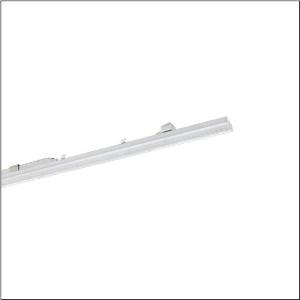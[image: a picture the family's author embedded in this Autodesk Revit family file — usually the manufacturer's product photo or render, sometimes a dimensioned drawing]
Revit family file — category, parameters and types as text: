
# Revit family: tl_l_5wd7a8p0g2b5
name_source: partatom
category: Lighting Fixtures
units: mm (PartAtom-declared; Revit-internal decimal feet)

## family parameters
Cut with Voids When Loaded = No
Host = Face
Light Source = No
Part Type = Normal
Room Calculation Point = No
Round Connector Dimension = Use Diameter
Shared = No

## types (1)
- --- (1 x LED, 5000 lm, 31.5 W, 4000K)
    Apparent Load = 32 VA
    CIE Flux Codes = 49 84 98 100 100
    Color Rendering = 80
    Color Temperature = 4000K
    Default Elevation = 1800 mm
    Description = TL L, luminaire insert, of sheet steel, galvanised, coil coated, white, length: 1.500mm, width: 66mm, height: 67mm, surge protection,LED light colour: 840, control gear: DALI, with terminal, 5-pole, mains connection: 230..240V, AC, 50/60Hz, rated input power: 63W, primary optical cover: cover, of PMMA, light emission: direct distribution, protection rating (complete): as luminaire, insulation class (complete): insulation class I (protective earthing), certification: CE, impact resistance: IK06, permissible ambient temperature for indoor applications: -35..+35°C, standard: NMF01, packaging unit: 1 piece
    Height = 120 mm
    Lamp = 1 x LED
    Lamp Light Flux = 5000 lm
    Lamp Power = 31.5 W
    Lamp count = 1
    Length = 1690 mm
    Luminous efficacy = 159 lm/W
    Manufacturer = Siteco
    ModVariant = No
    Model = 5WD7A8P0G2B5
    Mounting Place = Ceiling
    Mounting Type = Pendant
    Number of Poles = 1
    OnlyDefault = Yes
    Power Factor = 1
    Product Name = TL L
    Product group = luminaire insert
    ProductGroupID = 901
    Protection Class = Protection class I
    Protection Degree = Degree of protection
    RLX_Detail_Level = 1
    RLX_Emergency_Light_Flux = 0 lm
    RLX_Emergency_Type = 0
    RLX_Emergency_Type_DB = No
    RlxData = <blob elided: 17361 chars, md5=f54e580c>
    Socket = socket
    Standby Power = 0 W
    System Light Flux = 5000 lm
    System Power = 32 W
    Type Comments = factory setting: luminous flux: 100 % | dim-lin: 254 | 646 mA
    Type Image = l_1294382.jpg
    URL = http://relux.com
    VarID = @adj_000467
    Voltage = 0 V
    Weight = 0.00 kg
    Width = 208 mm

## geometry (parser evidence)
native form markers: Blend x4, Sweep x12
no freeform markers — native parametric forms only
